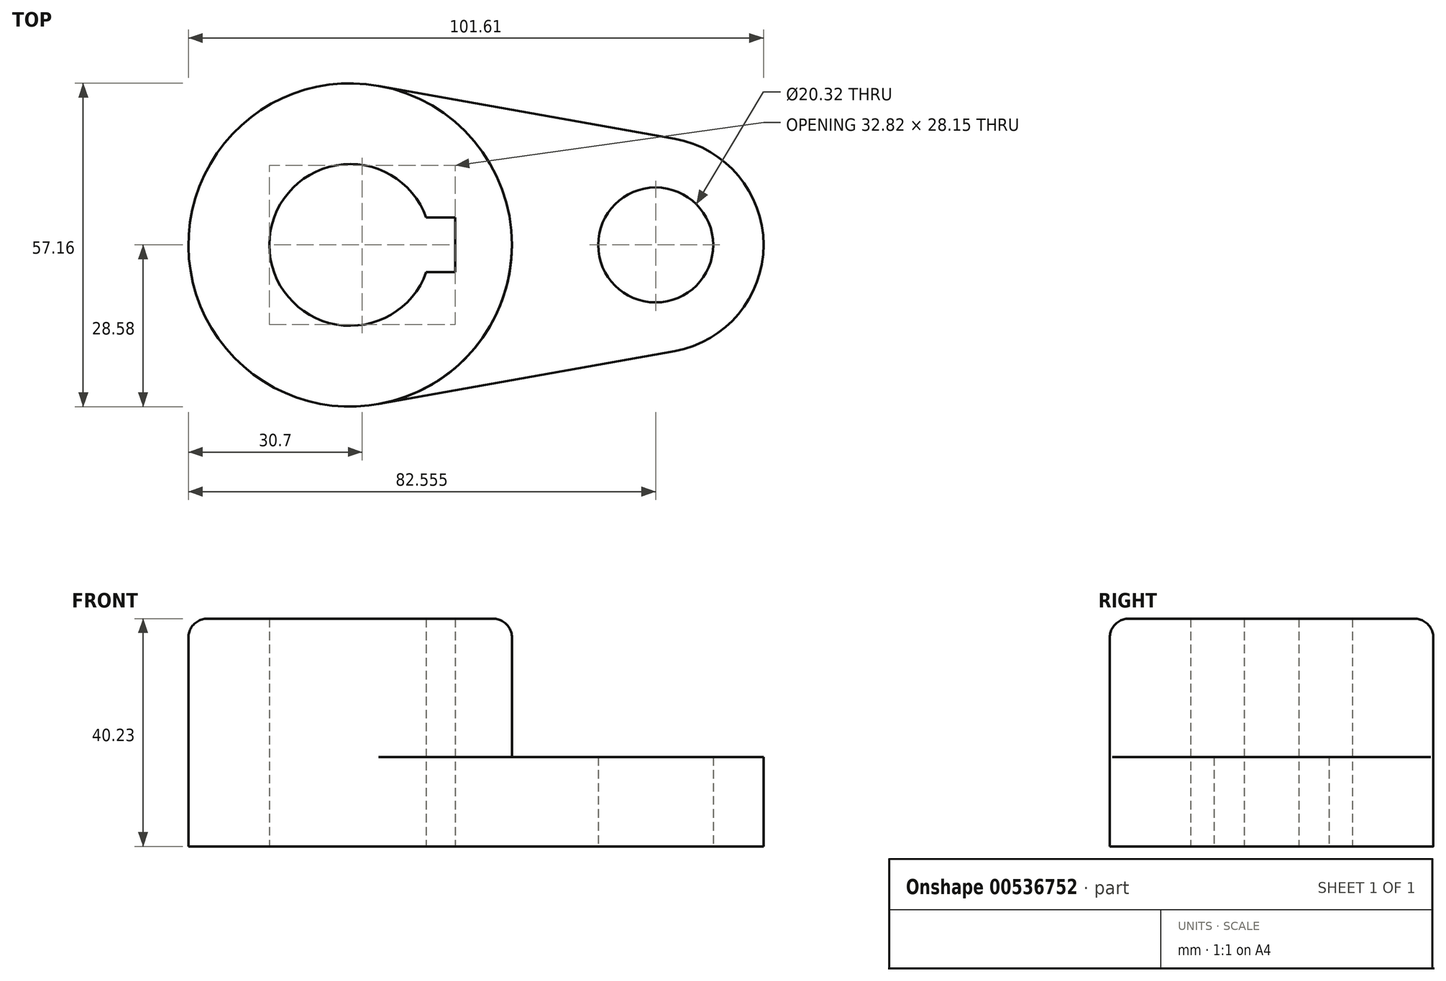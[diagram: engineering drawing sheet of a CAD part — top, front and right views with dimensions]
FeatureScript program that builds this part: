
annotation { "Feature Type Name" : "Feature", "Feature Type Description" : "" }
export const myFeature = defineFeature(function(context is Context, id is Id, definition is map)
    precondition{}
    {
        {
            var Q0;
            Q0=qCreatedBy(makeId("Top.planeOp"),FACE);
            var sketch = newSketch(context, id + "F0", { "sketchPlane" : qUnion([Q0])});
            skArc(sketch, "E0", {"start": v(57.34, -18.75) * mm, "mid": v(73.03, 0) * mm, "end": v(57.34, 18.75) * mm});
            skCircle(sketch, "E1", {"center": v(0, 0) * mm, "radius": 28.58 * mm});
            skLineSegment(sketch, "E2", {"start": v(5.04, 28.13) * mm, "end": v(57.34, 18.75) * mm});
            skLineSegment(sketch, "E3", {"start": v(5.04, -28.13) * mm, "end": v(57.34, -18.75) * mm});
            skArc(sketch, "E4", {"start": v(13.45, 4.83) * mm, "mid": v(-14.29, 0) * mm, "end": v(13.45, -4.83) * mm});
            skCircle(sketch, "E5", {"center": v(53.98, 0) * mm, "radius": 10.16 * mm});
            skLineSegment(sketch, "E6", {"start": v(18.53, 4.83) * mm, "end": v(18.53, -4.83) * mm});
            skLineSegment(sketch, "E7", {"start": v(13.45, 4.83) * mm, "end": v(18.53, 4.83) * mm});
            skLineSegment(sketch, "E8", {"start": v(13.45, -4.83) * mm, "end": v(18.53, -4.83) * mm});
            skLineSegment(sketch, "E9", {"start": v(0, 0) * mm, "end": v(18.53, 0) * mm, "construction": true});
            skSolve(sketch);
        }
        {
            var Q0;
            Q0=makeQuery(id+"F0.imprint","IMPRINT",FACE,{"disambiguationData":[TD([[makeQuery(id+"F0.imprint","IMPRINT",EDGE,{"derivedFrom":sQuery(id+"F0.wireOp",EDGE,"E0")}),1.0]])]});
            extrude(context, id + "F1", {"entities" : qUnion([Q0]), "depth" : 15.77 * mm, "offsetDistance" : 25.4 * mm});
        }
        {
            var Q0;
            Q0=makeQuery(id+"F0.imprint","IMPRINT",FACE,{"disambiguationData":[TD([[makeQuery(id+"F0.imprint","IMPRINT",EDGE,{"derivedFrom":sQuery(id+"F0.wireOp",EDGE,"E4")}),-1.0]])]});
            extrude(context, id + "F2", {"entities" : qUnion([Q0]), "operationType" : NewBodyOperationType.ADD, "depth" : 40.23 * mm, "offsetDistance" : 25.4 * mm});
        }
        {
            var Q0;
            Q0=makeQuery(id+"F2.opExtrude","CAP_EDGE",EDGE,{"disambiguationData":[OSD([sQuery(id+"F0.wireOp",EDGE,"E1")])],"isStart":false});
            fillet(context, id + "F3", {"entities" : qUnion([Q0]), "radius" : 3.3 * mm, "tangentPropagation" : true, "allowEdgeOverflow" : false});
        }
    });
